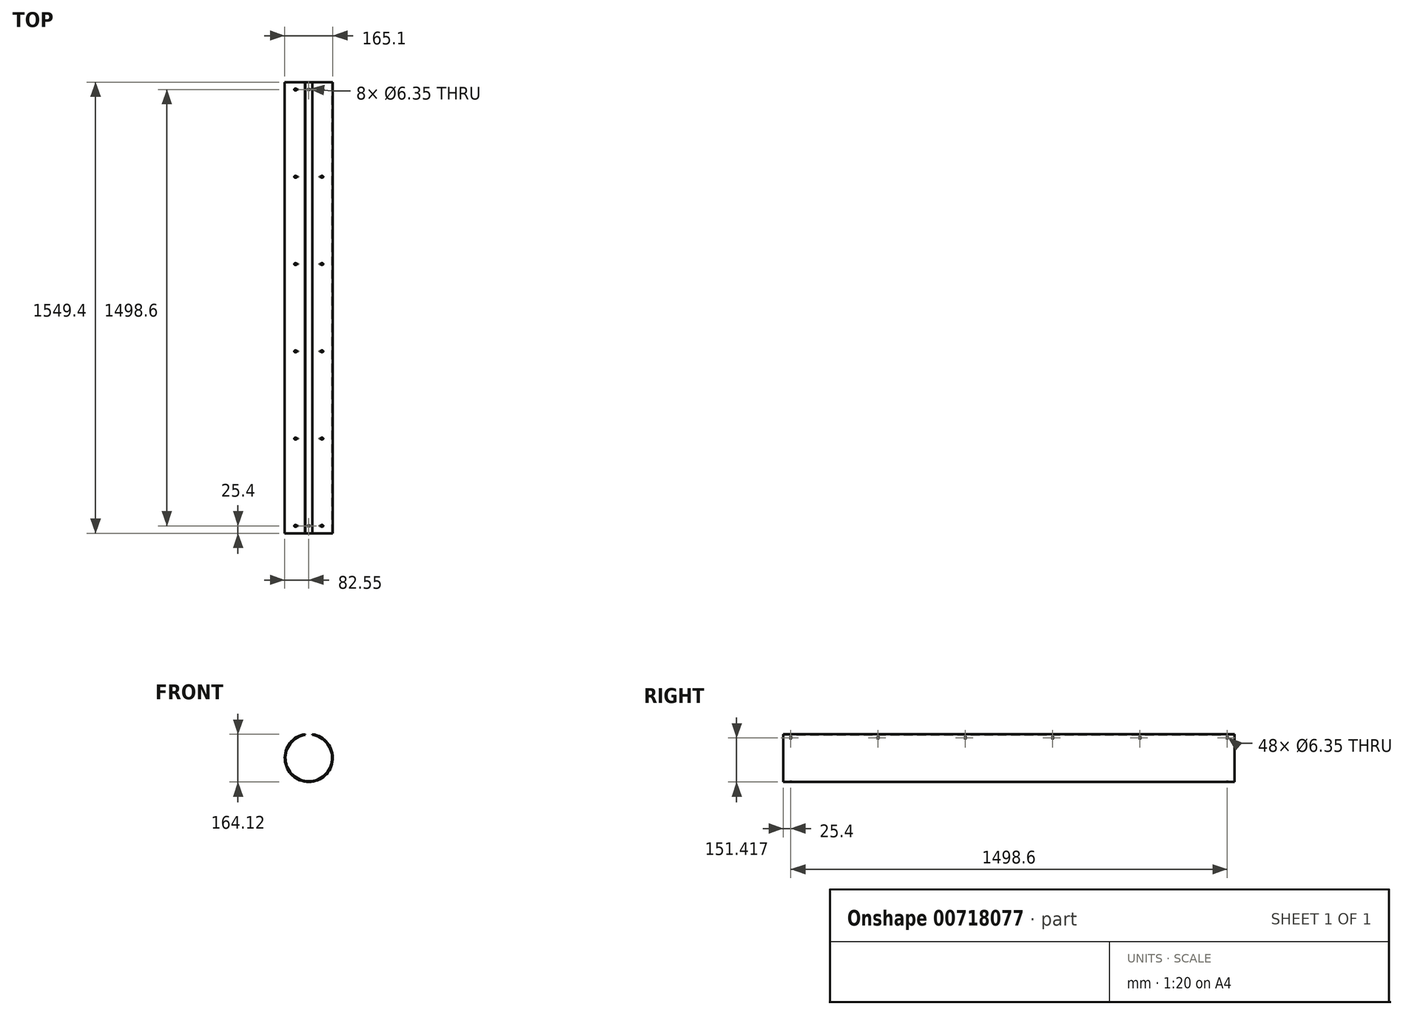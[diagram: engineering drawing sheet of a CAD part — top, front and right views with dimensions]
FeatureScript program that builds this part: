
annotation { "Feature Type Name" : "Feature", "Feature Type Description" : "" }
export const myFeature = defineFeature(function(context is Context, id is Id, definition is map)
    precondition{}
    {
        {
            var Q0;
            Q0=qCreatedBy(makeId("Front.planeOp"),FACE);
            var sketch = newSketch(context, id + "F0", { "sketchPlane" : qUnion([Q0])});
            skArc(sketch, "E0", {"start": v(-12.7, 81.57) * mm, "mid": v(0, -82.55) * mm, "end": v(12.7, 81.57) * mm});
            skArc(sketch, "E1", {"start": v(-12.3, 79.06) * mm, "mid": v(0, -80) * mm, "end": v(12.3, 79.06) * mm});
            skLineSegment(sketch, "E2", {"start": v(12.3, 79.06) * mm, "end": v(12.7, 81.57) * mm});
            skLineSegment(sketch, "E3", {"start": v(-12.3, 79.06) * mm, "end": v(-12.7, 81.57) * mm});
            skPoint(sketch, "E4.orphan", {"position": v(0, 82.55) * mm});
            skSolve(sketch);
        }
        {
            var Q0;
            Q0 = qSketchRegion(id + "F0", true);
            extrude(context, id + "F1", {"entities" : qUnion([Q0]), "depth" : 1549.4 * mm, "offsetDistance" : 25.4 * mm});
        }
        {
            var Q0;
            Q0=qCreatedBy(makeId("Top.planeOp"),FACE);
            var sketch = newSketch(context, id + "F2", { "sketchPlane" : qUnion([Q0])});
            skLineSegment(sketch, "E5", {"start": v(0, 0) * mm, "end": v(0, -1549.4) * mm, "construction": true});
            skCircle(sketch, "E6", {"center": v(0, -25.4) * mm, "radius": 3.18 * mm});
            skCircle(sketch, "E7", {"center": v(0, -1524) * mm, "radius": 3.17 * mm});
            skSolve(sketch);
        }
        {
            var Q0;
            Q0 = qSketchRegion(id + "F2", true);
            extrude(context, id + "F3", {"entities" : qUnion([Q0]), "operationType" : NewBodyOperationType.REMOVE, "endBound" : BoundingType.SYMMETRIC, "oppositeDirection" : true, "depth" : 254 * mm, "offsetDistance" : 25.4 * mm});
        }
        {
            var Q0;
            Q0=qCreatedBy(makeId("Right.planeOp"),FACE);
            var sketch = newSketch(context, id + "F4", { "sketchPlane" : qUnion([Q0])});
            skLineSegment(sketch, "E8", {"start": v(0, 0) * mm, "end": v(0, 129.89) * mm, "construction": true});
            skLineSegment(sketch, "E9.0", {"start": v(-1549.4, 81.57) * mm, "end": v(0, 81.57) * mm});
            skLineSegment(sketch, "E10", {"start": v(0, 0) * mm, "end": v(0, 81.57) * mm, "construction": true});
            skLineSegment(sketch, "E11", {"start": v(0, 68.87) * mm, "end": v(-75.02, 68.87) * mm, "construction": true});
            skCircle(sketch, "E12", {"center": v(-25.4, 68.87) * mm, "radius": 3.17 * mm});
            skCircle(sketch, "E13", {"center": v(-325.12, 68.87) * mm, "radius": 3.18 * mm});
            skCircle(sketch, "E14", {"center": v(-624.84, 68.87) * mm, "radius": 3.18 * mm});
            skCircle(sketch, "E15", {"center": v(-924.56, 68.87) * mm, "radius": 3.18 * mm});
            skCircle(sketch, "E16", {"center": v(-1224.28, 68.87) * mm, "radius": 3.18 * mm});
            skCircle(sketch, "E17", {"center": v(-1524, 68.87) * mm, "radius": 3.18 * mm});
            skSolve(sketch);
        }
        {
            var Q0;
            Q0 = qSketchRegion(id + "F4", true);
            extrude(context, id + "F5", {"entities" : qUnion([Q0]), "operationType" : NewBodyOperationType.REMOVE, "endBound" : BoundingType.SYMMETRIC, "oppositeDirection" : true, "depth" : 254 * mm, "offsetDistance" : 25.4 * mm});
        }
    });
